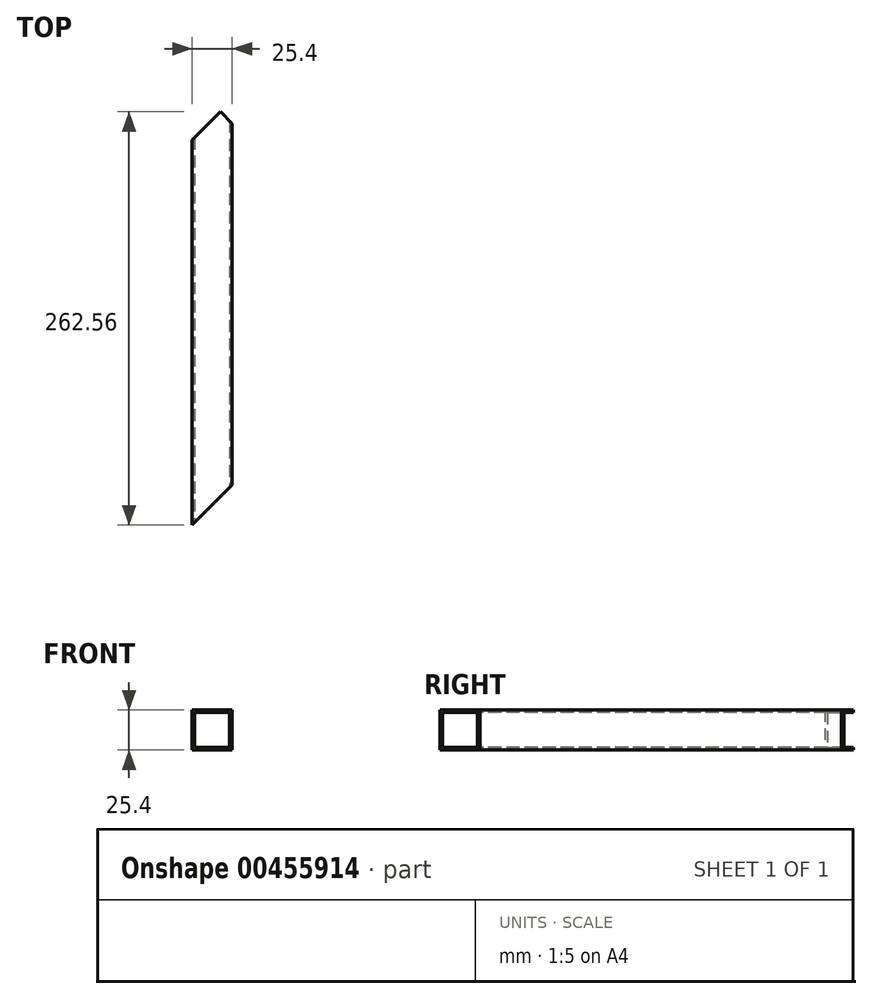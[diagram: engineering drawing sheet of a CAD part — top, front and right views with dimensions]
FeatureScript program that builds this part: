
annotation { "Feature Type Name" : "Feature", "Feature Type Description" : "" }
export const myFeature = defineFeature(function(context is Context, id is Id, definition is map)
    precondition{}
    {
        {
            var Q0;
            Q0=qCreatedBy(makeId("Top.planeOp"),FACE);
            var sketch = newSketch(context, id + "F0", { "sketchPlane" : qUnion([Q0])});
            skLineSegment(sketch, "E0.bottom", {"start": v(-12.7, 135) * mm, "end": v(12.7, 135) * mm});
            skLineSegment(sketch, "E0.top", {"start": v(-12.7, -135) * mm, "end": v(12.7, -135) * mm});
            skLineSegment(sketch, "E0.left", {"start": v(-12.7, 135) * mm, "end": v(-12.7, -135) * mm});
            skLineSegment(sketch, "E0.right", {"start": v(12.7, 135) * mm, "end": v(12.7, -135) * mm});
            skPoint(sketch, "E0.middle", {"position": v(0, 0) * mm});
            skLineSegment(sketch, "E1", {"start": v(12.7, 135) * mm, "end": v(-12.7, 109.6) * mm});
            skPoint(sketch, "E2", {"position": v(5.26, 127.56) * mm});
            skLineSegment(sketch, "E3", {"start": v(5.26, 127.56) * mm, "end": v(12.7, 120.12) * mm});
            skSolve(sketch);
        }
        {
            var Q0;
            {var subQ0=sQuery(id+"F0.wireOp",EDGE,"E3");Q0=makeQuery(id+"F0.imprint","IMPRINT",FACE,{"disambiguationData":[TD([[makeQuery(id+"F0.imprint","IMPRINT",EDGE,{"derivedFrom":subQ0}),-1.0]])]});}
            extrude(context, id + "F1", {"entities" : qUnion([Q0]), "depth" : 25.4 * mm});
        }
        {
            var Q0;
            Q0=makeQuery(id+"F1.opExtrude","SWEPT_FACE",FACE,{"disambiguationData":[OSD([sQuery(id+"F0.wireOp",EDGE,"E0.top")])]});
            shell(context, id + "F2", {"entities" : qUnion([Q0]), "thickness" : 1.59 * mm});
        }
        {
            var Q0;
            Q0=makeQuery(id+"F1.opExtrude","SWEPT_FACE",FACE,{"disambiguationData":[OSD([sQuery(id+"F0.wireOp",EDGE,"E0.top")])]});
            var sketch = newSketch(context, id + "F3", { "sketchPlane" : qUnion([Q0])});
            skLineSegment(sketch, "E4.bottom", {"start": v(-11.11, 23.81) * mm, "end": v(11.11, 23.81) * mm});
            skLineSegment(sketch, "E4.top", {"start": v(-11.11, 1.59) * mm, "end": v(11.11, 1.59) * mm});
            skLineSegment(sketch, "E4.left", {"start": v(-11.11, 23.81) * mm, "end": v(-11.11, 1.59) * mm});
            skLineSegment(sketch, "E4.right", {"start": v(11.11, 23.81) * mm, "end": v(11.11, 1.59) * mm});
            skSolve(sketch);
        }
        {
            var Q0;
            Q0 = qSketchRegion(id + "F3", true);
            extrude(context, id + "F4", {"entities" : qUnion([Q0]), "operationType" : NewBodyOperationType.REMOVE, "endBound" : BoundingType.THROUGH_ALL, "oppositeDirection" : true, "depth" : 25.4 * mm});
        }
        {
            var Q0;
            Q0=makeQuery(id+"F1.opExtrude","CAP_FACE",FACE,{"disambiguationData":[OSD([sQuery(id+"F0.wireOp",EDGE,"E0.top"),sQuery(id+"F0.wireOp",EDGE,"E0.left"),sQuery(id+"F0.wireOp",EDGE,"E0.right"),sQuery(id+"F0.wireOp",EDGE,"E1"),sQuery(id+"F0.wireOp",EDGE,"E3")])],"isStart":false});
            var sketch = newSketch(context, id + "F5", { "sketchPlane" : qUnion([Q0])});
            skLineSegment(sketch, "E5", {"start": v(-12.7, -135) * mm, "end": v(12.7, -109.6) * mm});
            skSolve(sketch);
        }
        {
            var Q0;
            {var subQ0=sQuery(id+"F5.wireOp",EDGE,"E5");Q0=makeQuery(id+"F5.imprint","IMPRINT",FACE,{"disambiguationData":[TD([[makeQuery(id+"F5.imprint","IMPRINT",EDGE,{"derivedFrom":subQ0}),-1.0]])]});}
            extrude(context, id + "F6", {"entities" : qUnion([Q0]), "operationType" : NewBodyOperationType.REMOVE, "oppositeDirection" : true, "depth" : 25.4 * mm});
        }
    });
